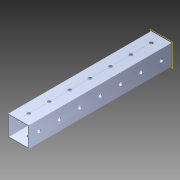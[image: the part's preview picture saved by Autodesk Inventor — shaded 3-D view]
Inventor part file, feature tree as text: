
AUTODESK INVENTOR PART (.ipt)
format: ipt  version: 2014 (Build 180170000, 170)  size: 1,158,656 bytes
history: native  units: in
note: dims shown in document units (in); Inventor stores cm internally (conversion verified against a paired STEP export)
features: pattern_circular x1, other x1, plane x1, extrude x1, imported_body x1, sketch x1
ambient origin geometry x8: Origin, YZ Plane, XZ Plane, XY Plane, X Axis, Y Axis, Z Axis, Center Point
bodies: Body1 (feature_tree)
feature tree (6):
  pattern_circular  "CirPattern2"
  other  "217-3426-STEP1"
  plane  "Work Plane1"
  extrude  "Extrusion1"  Depth=3937.0079in TaperAngle=0.0deg
  imported_body  "Base1"
  sketch  "Sketch1"  dims[d0=-7.0in d1=3937.0079in d2=0.0in]
